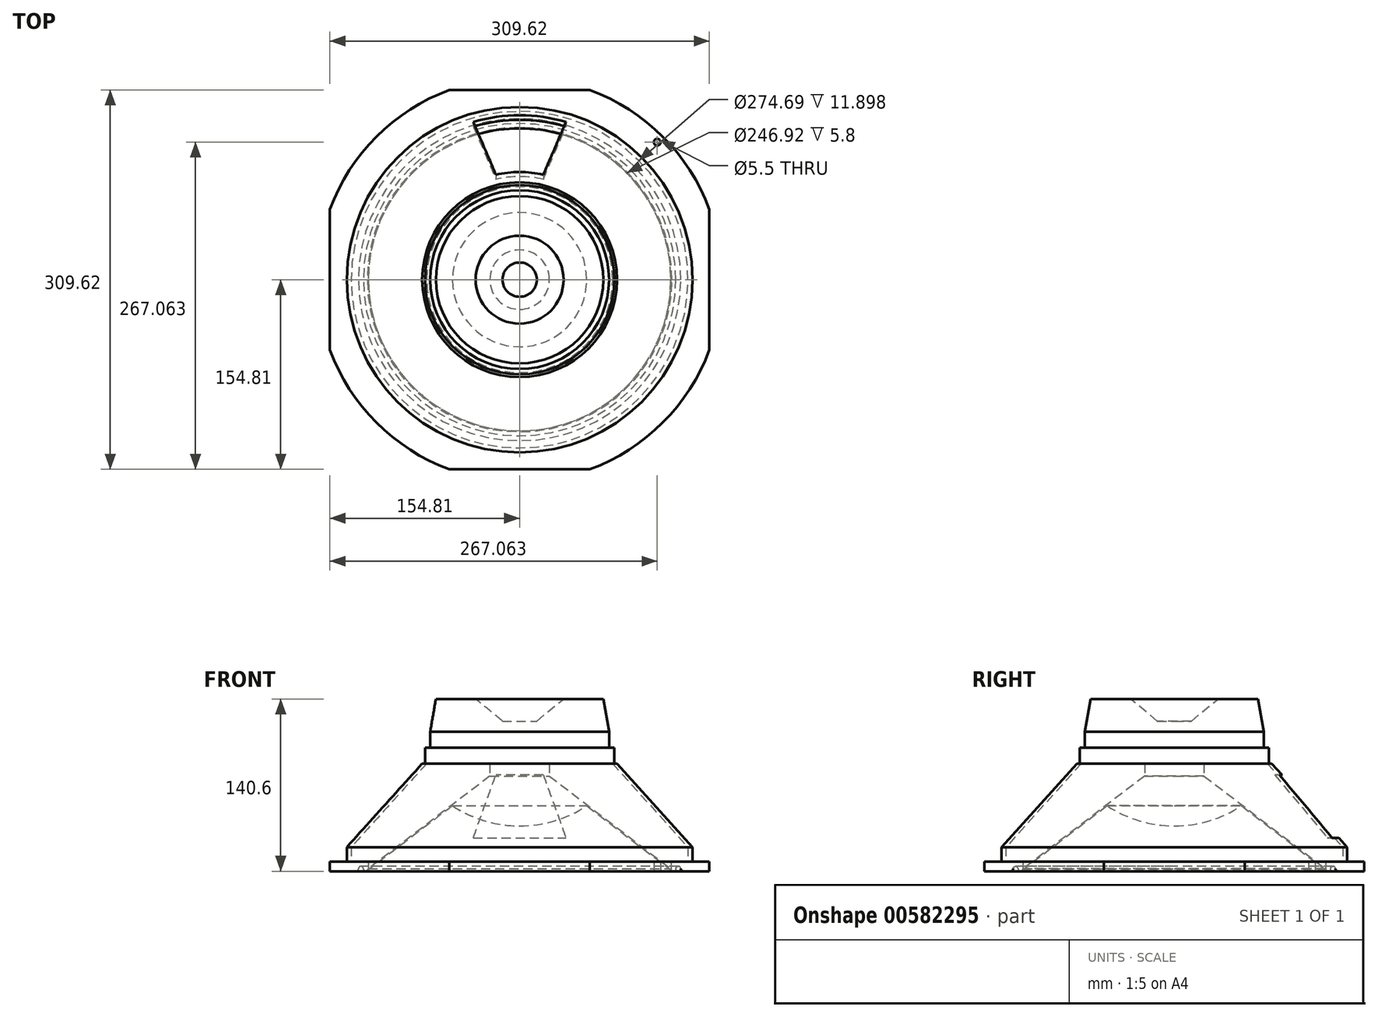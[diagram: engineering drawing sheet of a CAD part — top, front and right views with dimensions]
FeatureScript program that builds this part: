
annotation { "Feature Type Name" : "Feature", "Feature Type Description" : "" }
export const myFeature = defineFeature(function(context is Context, id is Id, definition is map)
    precondition{}
    {
        {
            var Q0;
            Q0=qCreatedBy(makeId("Top.planeOp"),FACE);
            var sketch = newSketch(context, id + "F0", { "sketchPlane" : qUnion([Q0])});
            skCircle(sketch, "E0", {"center": v(0, 0) * mm, "radius": 165.1 * mm, "construction": true});
            skLineSegment(sketch, "E1", {"start": v(0, 0) * mm, "end": v(-154.8, 0) * mm, "construction": true});
            skCircle(sketch, "E2", {"center": v(0, 0) * mm, "radius": 54.77 * mm, "construction": true});
            skCircle(sketch, "E3", {"center": v(0, 0) * mm, "radius": 123.46 * mm, "construction": true});
            skCircle(sketch, "E4", {"center": v(0, 0) * mm, "radius": 142.6 * mm, "construction": true});
            skCircle(sketch, "E5", {"center": v(0, 0) * mm, "radius": 152.26 * mm, "construction": true});
            skLineSegment(sketch, "E6.bottom", {"start": v(-154.8, 154.81) * mm, "end": v(154.8, 154.81) * mm});
            skLineSegment(sketch, "E6.top", {"start": v(-154.81, -154.81) * mm, "end": v(154.81, -154.81) * mm});
            skLineSegment(sketch, "E6.left", {"start": v(-154.81, 154.8) * mm, "end": v(-154.81, -154.81) * mm});
            skLineSegment(sketch, "E6.right", {"start": v(154.8, 154.8) * mm, "end": v(154.8, -154.81) * mm});
            skLineSegment(sketch, "E7", {"start": v(0, 0) * mm, "end": v(0, 193.71) * mm, "construction": true});
            skCircle(sketch, "E8", {"center": v(0, 0) * mm, "radius": 158.75 * mm, "construction": true});
            skSolve(sketch);
        }
        {
            var Q0;
            Q0=qCreatedBy(makeId("Front.planeOp"),FACE);
            var sketch = newSketch(context, id + "F1", { "sketchPlane" : qUnion([Q0])});
            skLineSegment(sketch, "E9", {"start": v(0, 0) * mm, "end": v(0, 128.72) * mm, "construction": true});
            skLineSegment(sketch, "E10", {"start": v(35.88, 140.6) * mm, "end": v(68.28, 140.6) * mm});
            skLineSegment(sketch, "E11", {"start": v(165.1, 0) * mm, "end": v(165.1, 7.8) * mm});
            skLineSegment(sketch, "E12", {"start": v(165.1, 7.8) * mm, "end": v(141, 7.8) * mm});
            skLineSegment(sketch, "E13", {"start": v(141, 7.8) * mm, "end": v(141, 19.7) * mm});
            skLineSegment(sketch, "E14", {"start": v(141, 19.7) * mm, "end": v(79.47, 87.83) * mm});
            skLineSegment(sketch, "E15", {"start": v(79.47, 87.83) * mm, "end": v(77.22, 87.83) * mm});
            skLineSegment(sketch, "E16", {"start": v(77.22, 87.83) * mm, "end": v(77.22, 100.9) * mm});
            skLineSegment(sketch, "E17", {"start": v(77.22, 100.9) * mm, "end": v(72.97, 100.9) * mm});
            skLineSegment(sketch, "E18", {"start": v(72.97, 100.9) * mm, "end": v(72.97, 113.96) * mm});
            skLineSegment(sketch, "E19", {"start": v(72.97, 113.96) * mm, "end": v(68.28, 140.6) * mm});
            skLineSegment(sketch, "E20", {"start": v(35.88, 140.6) * mm, "end": v(14, 122.6) * mm});
            skLineSegment(sketch, "E21", {"start": v(14, 122.6) * mm, "end": v(0, 122.6) * mm});
            skLineSegment(sketch, "E22", {"start": v(0, 122.6) * mm, "end": v(0, 0) * mm});
            skLineSegment(sketch, "E23", {"start": v(54.77, 53.4) * mm, "end": v(54.77, 0) * mm, "construction": true});
            skArc(sketch, "E24", {"start": v(54.77, 53.4) * mm, "mid": v(28.59, 41.18) * mm, "end": v(0, 36.99) * mm});
            skLineSegment(sketch, "E25", {"start": v(123.46, 2) * mm, "end": v(123.46, 7.8) * mm});
            skLineSegment(sketch, "E26", {"start": v(123.46, 7.8) * mm, "end": v(137.34, 7.8) * mm});
            skLineSegment(sketch, "E27", {"start": v(137.34, 7.8) * mm, "end": v(137.34, 19.7) * mm});
            skLineSegment(sketch, "E28", {"start": v(137.34, 19.7) * mm, "end": v(75.81, 87.83) * mm});
            skLineSegment(sketch, "E29", {"start": v(75.81, 87.83) * mm, "end": v(0, 87.83) * mm});
            skArc(sketch, "E30", {"start": v(123.46, 2) * mm, "mid": v(125.46, 0) * mm, "end": v(127.46, 2) * mm});
            skArc(sketch, "E31", {"start": v(131.46, 2) * mm, "mid": v(129.46, 4) * mm, "end": v(127.46, 2) * mm});
            skArc(sketch, "E32", {"start": v(131.46, 2) * mm, "mid": v(132.05, 0.59) * mm, "end": v(133.46, 0) * mm});
            skLineSegment(sketch, "E33.trimOffspring", {"start": v(133.46, 0) * mm, "end": v(165.1, 0) * mm});
            skLineSegment(sketch, "E34", {"start": v(54.77, 53.4) * mm, "end": v(124.25, 0.4) * mm});
            skLineSegment(sketch, "E35", {"start": v(123.46, 2) * mm, "end": v(24.24, 77.67) * mm});
            skLineSegment(sketch, "E36", {"start": v(19.4, 78.6) * mm, "end": v(-19.4, 78.6) * mm});
            skLineSegment(sketch, "E37", {"start": v(-19.4, 78.6) * mm, "end": v(-37.76, 27.29) * mm});
            skLineSegment(sketch, "E38", {"start": v(-37.76, 27.29) * mm, "end": v(37.76, 27.29) * mm});
            skLineSegment(sketch, "E39", {"start": v(37.76, 27.29) * mm, "end": v(19.4, 78.6) * mm});
            skLineSegment(sketch, "E40", {"start": v(24.24, 77.67) * mm, "end": v(24.24, 87.83) * mm});
            skLineSegment(sketch, "E41", {"start": v(24.24, 87.83) * mm, "end": v(0, 87.83) * mm});
            skLineSegment(sketch, "E42", {"start": v(0, 36.99) * mm, "end": v(0, 87.83) * mm});
            skSolve(sketch);
        }
        {
            var Q0;
            Q0=makeQuery(id+"F1.imprint","IMPRINT",FACE,{"disambiguationData":[TD([[makeQuery(id+"F1.imprint","IMPRINT",EDGE,{"derivedFrom":sQuery(id+"F1.wireOp",EDGE,"E10")}),-1.0]])]});
            var Q1;
            Q1=sQuery(id+"F1.wireOp",EDGE,"E9");
            revolve(context, id + "F2", {"entities" : qUnion([Q0]), "axis" : qUnion([Q1]), "revolveType" : RevolveType.FULL});
        }
        {
            var Q0;
            Q0=makeQuery(id+"F0.imprint","IMPRINT",FACE,{"disambiguationData":[TD([[makeQuery(id+"F0.imprint","IMPRINT",EDGE,{"derivedFrom":sQuery(id+"F0.wireOp",EDGE,"E6.bottom")}),-1.0]])]});
            extrude(context, id + "F3", {"entities" : qUnion([Q0]), "operationType" : NewBodyOperationType.INTERSECT, "endBound" : BoundingType.THROUGH_ALL, "depth" : 25 * mm, "offsetDistance" : 25 * mm});
        }
        {
            var Q0;
            Q0=makeQuery(id+"F2.opRevolve","SWEPT_FACE",FACE,{"disambiguationData":[OSD([sQuery(id+"F1.wireOp",EDGE,"E33.trimOffspring")])]});
            var sketch = newSketch(context, id + "F4", { "sketchPlane" : qUnion([Q0])});
            skCircle(sketch, "E43", {"center": v(0, 0) * mm, "radius": 158.75 * mm, "construction": true});
            skLineSegment(sketch, "E44", {"start": v(0, 0) * mm, "end": v(112.25, -112.25) * mm, "construction": true});
            skSolve(sketch);
        }
        {
            var Q0;
            Q0=sQuery(id+"F4.wireOp",VERTEX,"E44.end");
            var Q1;
            Q1=makeQuery(id+"F2.opRevolve","SWEPT_BODY",BODY,{"disambiguationData":[OSD([sQuery(id+"F1.wireOp",EDGE,"E10"),sQuery(id+"F1.wireOp",EDGE,"E11"),sQuery(id+"F1.wireOp",EDGE,"E12"),sQuery(id+"F1.wireOp",EDGE,"E13"),sQuery(id+"F1.wireOp",EDGE,"E14"),sQuery(id+"F1.wireOp",EDGE,"E15"),sQuery(id+"F1.wireOp",EDGE,"E16"),sQuery(id+"F1.wireOp",EDGE,"E17"),sQuery(id+"F1.wireOp",EDGE,"E18"),sQuery(id+"F1.wireOp",EDGE,"E19"),sQuery(id+"F1.wireOp",EDGE,"E20"),sQuery(id+"F1.wireOp",EDGE,"E21"),sQuery(id+"F1.wireOp",EDGE,"E22"),sQuery(id+"F1.wireOp",EDGE,"E25"),sQuery(id+"F1.wireOp",EDGE,"E26"),sQuery(id+"F1.wireOp",EDGE,"E27"),sQuery(id+"F1.wireOp",EDGE,"E28"),sQuery(id+"F1.wireOp",EDGE,"E29"),sQuery(id+"F1.wireOp",EDGE,"E30"),sQuery(id+"F1.wireOp",EDGE,"E31"),sQuery(id+"F1.wireOp",EDGE,"E32"),sQuery(id+"F1.wireOp",EDGE,"E33.trimOffspring")])]});
            hole(context, id + "F5", {"style" : HoleStyle.SIMPLE, "endStyle" : HoleEndStyle.THROUGH, "holeDiameter" : 5.5 * mm, "majorDiameter" : 5 * mm, "isTappedThrough" : true, "tappedDepth" : 12 * mm, "tapClearance" : 3, "locations" : qUnion([Q0]), "scope" : qUnion([Q1])});
        }
        {
            var Q0;
            {var subQ3=sQuery(id+"F1.wireOp",EDGE,"E39");var subQ5=sQuery(id+"F1.wireOp",EDGE,"E36");var subQ6=makeQuery(id+"F1.imprint","INTERSECT",VERTEX,{"derivedFrom":[subQ5,subQ3]});Q0=makeQuery(id+"F1.imprint","IMPRINT",FACE,{"disambiguationData":[TD([[makeQuery(id+"F1.imprint","IMPRINT",EDGE,{"disambiguationData":[TD([[subQ6,-1.0]])],"derivedFrom":subQ5}),1.0]])]});}
            var Q1;
            {var subQ1=sQuery(id+"F1.wireOp",EDGE,"E37");Q1=makeQuery(id+"F1.imprint","IMPRINT",FACE,{"disambiguationData":[TD([[makeQuery(id+"F1.imprint","IMPRINT",EDGE,{"derivedFrom":subQ1}),1.0]])]});}
            var Q2;
            {var subQ3=sQuery(id+"F1.wireOp",EDGE,"E38");var subQ5=sQuery(id+"F1.wireOp",EDGE,"E39");var subQ6=makeQuery(id+"F1.imprint","INTERSECT",VERTEX,{"derivedFrom":[subQ3,subQ5]});Q2=makeQuery(id+"F1.imprint","IMPRINT",FACE,{"disambiguationData":[TD([[makeQuery(id+"F1.imprint","IMPRINT",EDGE,{"disambiguationData":[TD([[subQ6,1.0]])],"derivedFrom":subQ3}),1.0]])]});}
            extrude(context, id + "F6", {"entities" : qUnion([Q0, Q1, Q2]), "operationType" : NewBodyOperationType.REMOVE, "endBound" : BoundingType.THROUGH_ALL, "oppositeDirection" : true, "depth" : 25 * mm, "offsetDistance" : 25 * mm});
        }
        {
            var Q0;
            {var subQ5=sQuery(id+"F1.wireOp",EDGE,"E34");Q0=makeQuery(id+"F1.imprint","IMPRINT",FACE,{"disambiguationData":[TD([[makeQuery(id+"F1.imprint","IMPRINT",EDGE,{"derivedFrom":subQ5}),1.0]])]});}
            var Q1;
            {var subQ3=sQuery(id+"F1.wireOp",EDGE,"E39");var subQ5=sQuery(id+"F1.wireOp",EDGE,"E36");var subQ6=makeQuery(id+"F1.imprint","INTERSECT",VERTEX,{"derivedFrom":[subQ5,subQ3]});Q1=makeQuery(id+"F1.imprint","IMPRINT",FACE,{"disambiguationData":[TD([[makeQuery(id+"F1.imprint","IMPRINT",EDGE,{"disambiguationData":[TD([[subQ6,-1.0]])],"derivedFrom":subQ5}),1.0]])]});}
            var Q2;
            Q2=sQuery(id+"F1.wireOp",EDGE,"E9");
            revolve(context, id + "F7", {"entities" : qUnion([Q0, Q1]), "axis" : qUnion([Q2]), "revolveType" : RevolveType.FULL});
        }
    });
